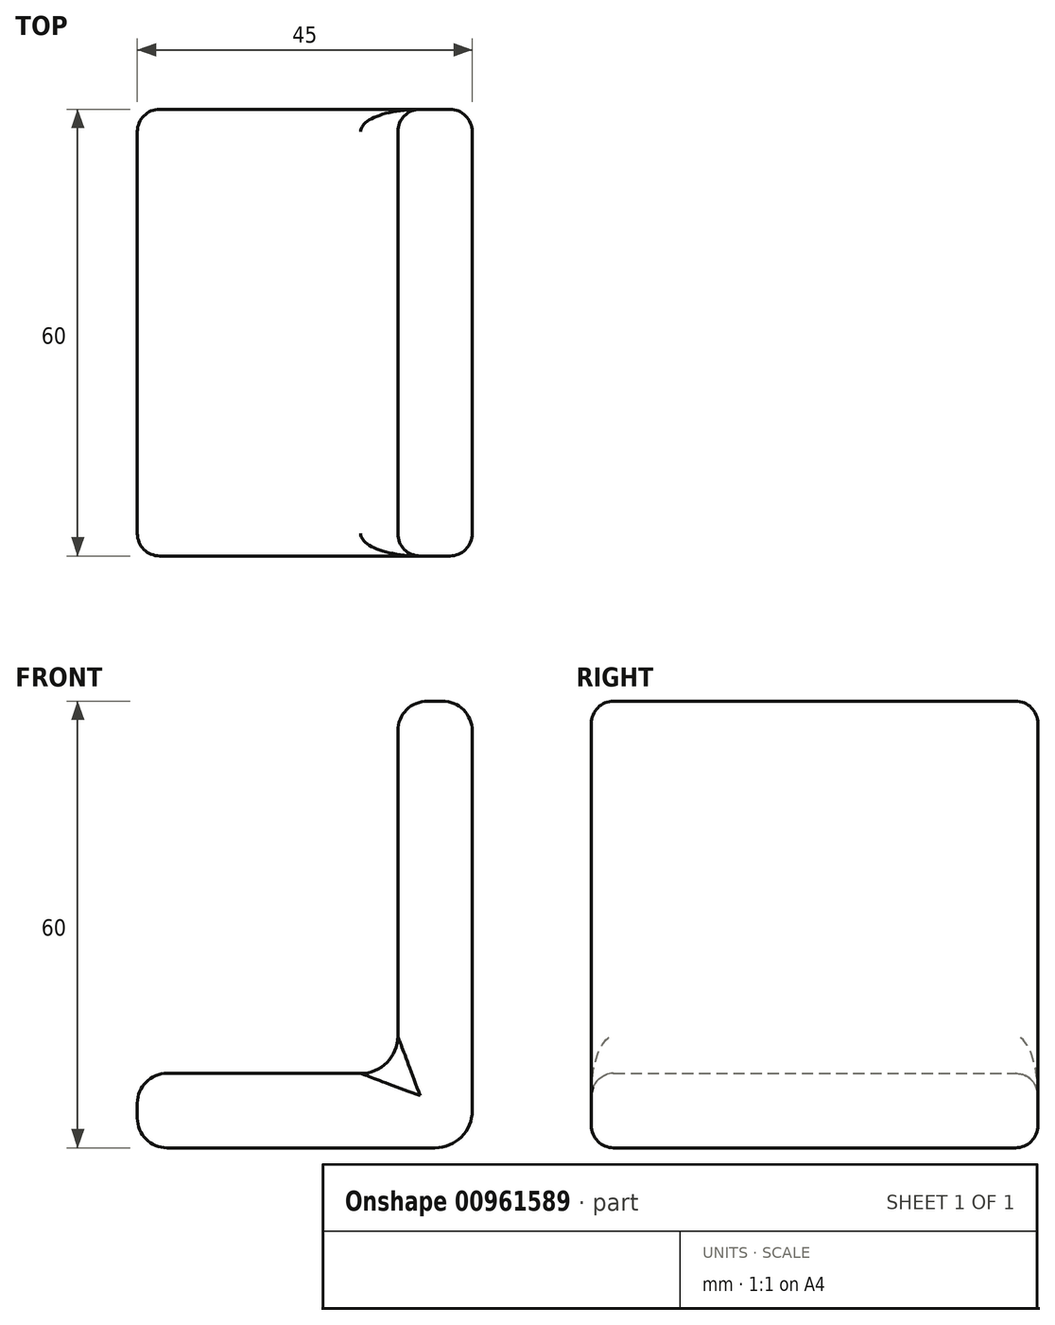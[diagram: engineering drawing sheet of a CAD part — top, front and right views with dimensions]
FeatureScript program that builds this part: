
annotation { "Feature Type Name" : "Feature", "Feature Type Description" : "" }
export const myFeature = defineFeature(function(context is Context, id is Id, definition is map)
    precondition{}
    {
        {
            var Q0;
            Q0=qCreatedBy(makeId("Front.planeOp"),FACE);
            var sketch = newSketch(context, id + "F0", { "sketchPlane" : qUnion([Q0])});
            skLineSegment(sketch, "E0", {"start": v(0, 0) * mm, "end": v(45, 0) * mm});
            skLineSegment(sketch, "E1", {"start": v(45, 0) * mm, "end": v(45, 60) * mm});
            skLineSegment(sketch, "E2", {"start": v(45, 60) * mm, "end": v(35, 60) * mm});
            skLineSegment(sketch, "E3", {"start": v(35, 60) * mm, "end": v(35, 10) * mm});
            skLineSegment(sketch, "E4", {"start": v(35, 10) * mm, "end": v(0, 10) * mm});
            skLineSegment(sketch, "E5", {"start": v(0, 10) * mm, "end": v(0, 0) * mm});
            skSolve(sketch);
        }
        {
            var Q0;
            Q0=makeQuery(id+"F0.imprint","IMPRINT",FACE,{"disambiguationData":[TD([[makeQuery(id+"F0.imprint","IMPRINT",EDGE,{"derivedFrom":sQuery(id+"F0.wireOp",EDGE,"E0")}),1.0]])]});
            extrude(context, id + "F1", {"entities" : qUnion([Q0]), "endBound" : BoundingType.SYMMETRIC, "depth" : 60 * mm, "offsetDistance" : 25 * mm});
        }
        {
            var Q0;
            Q0=makeQuery(id+"F1.opExtrude","SWEPT_EDGE",EDGE,{"disambiguationData":[OSD([sQuery(id+"F0.wireOp",EDGE,"E2"),sQuery(id+"F0.wireOp",EDGE,"E3")])]});
            var Q1;
            Q1=makeQuery(id+"F1.opExtrude","SWEPT_EDGE",EDGE,{"disambiguationData":[OSD([sQuery(id+"F0.wireOp",EDGE,"E1"),sQuery(id+"F0.wireOp",EDGE,"E2")])]});
            var Q2;
            Q2=makeQuery(id+"F1.opExtrude","SWEPT_EDGE",EDGE,{"disambiguationData":[OSD([sQuery(id+"F0.wireOp",EDGE,"E4"),sQuery(id+"F0.wireOp",EDGE,"E5")])]});
            var Q3;
            Q3=makeQuery(id+"F1.opExtrude","SWEPT_EDGE",EDGE,{"disambiguationData":[OSD([sQuery(id+"F0.wireOp",EDGE,"E0"),sQuery(id+"F0.wireOp",EDGE,"E5")])]});
            fillet(context, id + "F2", {"entities" : qUnion([Q0, Q1, Q2, Q3]), "radius" : 4 * mm, "tangentPropagation" : true, "allowEdgeOverflow" : false});
        }
        {
            var Q0;
            Q0=makeQuery(id+"F1.opExtrude","CAP_EDGE",EDGE,{"disambiguationData":[OSD([sQuery(id+"F0.wireOp",EDGE,"E3")])],"isStart":false});
            var Q1;
            Q1=makeQuery(id+"F1.opExtrude","CAP_EDGE",EDGE,{"disambiguationData":[OSD([sQuery(id+"F0.wireOp",EDGE,"E4")])],"isStart":false});
            var Q2;
            Q2=makeQuery(id+"F1.opExtrude","CAP_EDGE",EDGE,{"disambiguationData":[OSD([sQuery(id+"F0.wireOp",EDGE,"E3")])],"isStart":true});
            var Q3;
            Q3=makeQuery(id+"F1.opExtrude","CAP_EDGE",EDGE,{"disambiguationData":[OSD([sQuery(id+"F0.wireOp",EDGE,"E4")])],"isStart":true});
            fillet(context, id + "F3", {"entities" : qUnion([Q0, Q1, Q2, Q3]), "radius" : 3 * mm, "tangentPropagation" : true, "allowEdgeOverflow" : false});
        }
        {
            var Q0;
            Q0=makeQuery(id+"F1.opExtrude","SWEPT_EDGE",EDGE,{"disambiguationData":[OSD([sQuery(id+"F0.wireOp",EDGE,"E3"),sQuery(id+"F0.wireOp",EDGE,"E4")])]});
            var Q1;
            Q1=makeQuery(id+"F1.opExtrude","SWEPT_EDGE",EDGE,{"disambiguationData":[OSD([sQuery(id+"F0.wireOp",EDGE,"E0"),sQuery(id+"F0.wireOp",EDGE,"E1")])]});
            fillet(context, id + "F4", {"entities" : qUnion([Q0, Q1]), "radius" : 5 * mm, "tangentPropagation" : true, "allowEdgeOverflow" : false});
        }
    });
